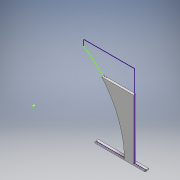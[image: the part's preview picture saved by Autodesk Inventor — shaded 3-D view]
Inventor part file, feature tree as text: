
AUTODESK INVENTOR PART (.ipt)
format: ipt  version: 2018 (Build 220112000, 112)  size: 1,238,528 bytes
history: native  units: mm
features: sketch x14, extrude x9, emboss x2
ambient origin geometry x8: Origin, YZ Plane, XZ Plane, XY Plane, X Axis, Y Axis, Z Axis, Center Point
bodies: Solid1 (feature_tree)
feature tree (25):
  extrude  "Extrusion1"  Depth=450.0mm
  extrude  "Extrusion2"  Depth=3.0mm
  extrude  "Extrusion3"  Depth=3.0mm
  extrude  "Extrusion4"  Depth=3.0mm TaperAngle=0.0deg
  extrude  "Extrusion5"  Depth=3.0mm
  extrude  "Extrusion6"  Depth=25.0mm TaperAngle=0.0deg
  emboss  "Emboss1"
  sketch  "Sketch8"  dims[d20=2.0mm d21=0.0mm d22=2.0mm d23=0.0mm]
  sketch  "Sketch9"  dims[d24=7.0mm d26=2.0mm d27=0.0mm]
  extrude  "Extrusion7"  Depth=2.0mm
  emboss  "Emboss2"
  extrude  "Extrusion8"  Depth=2.0mm TaperAngle=0.0deg
  extrude  "Extrusion9"  Depth=2.0mm TaperAngle=0.0deg
  sketch  "Sketch14"
  sketch  "Sketch1"  dims[d0=450.0mm d1=450.0mm]
  sketch  "Sketch2"  dims[d2=3.0mm d3=0.0mm d4=410.0mm]
  sketch  "Sketch3"  dims[d5=3.0mm d6=0.0mm d7=112.5mm]
  sketch  "Sketch4"  dims[d8=3.0mm d9=0.0mm d10=3.0mm d11=0.0mm]
  sketch  "Sketch5"  dims[d12=85.0mm d13=3.0mm]
  sketch  "Sketch6"  dims[d14=6.0mm d15=0.0mm d16=25.0mm d17=0.0mm]
  sketch  "Sketch7"  dims[d18=2.0mm d19=2.0mm]
  sketch  "Sketch10"  dims[d28=2.0mm d29=0.0mm]
  sketch  "Sketch11"  dims[d30=50.0mm]
  sketch  "Sketch12"  dims[d31=5.0mm d32=0.0mm]
  sketch  "Sketch13"
